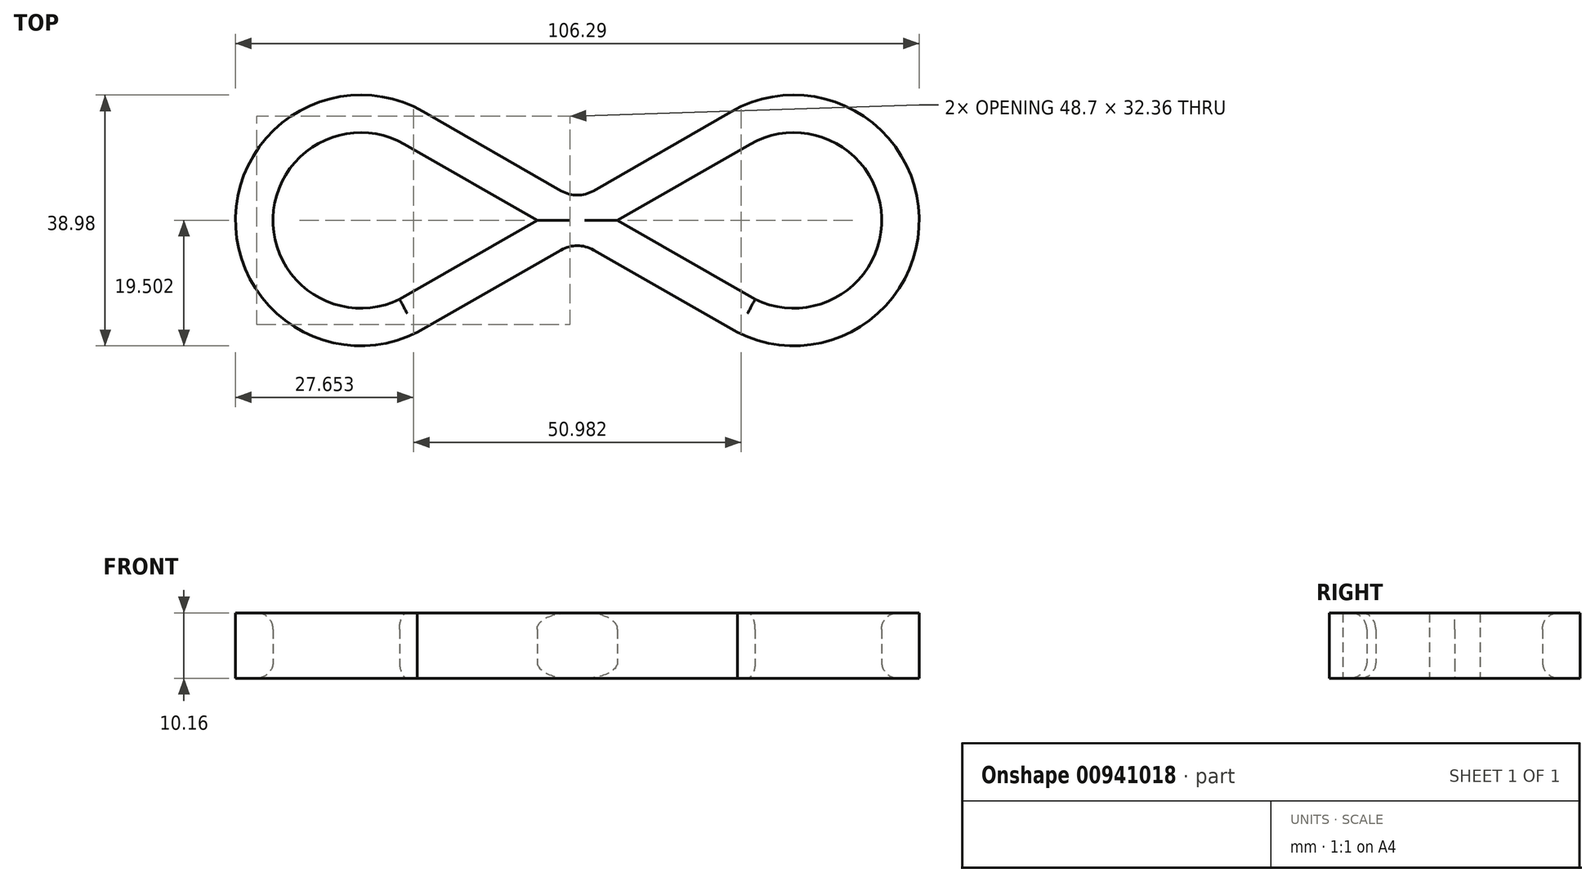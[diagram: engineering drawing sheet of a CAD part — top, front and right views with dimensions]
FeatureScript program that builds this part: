
annotation { "Feature Type Name" : "Feature", "Feature Type Description" : "" }
export const myFeature = defineFeature(function(context is Context, id is Id, definition is map)
    precondition{}
    {
        {
            var Q0;
            Q0=qCreatedBy(makeId("Top.planeOp"),FACE);
            var sketch = newSketch(context, id + "F0", { "sketchPlane" : qUnion([Q0])});
            skArc(sketch, "E0", {"start": v(6.8, 11.84) * mm, "mid": v(-13.64, 0.44) * mm, "end": v(6.02, -12.25) * mm});
            skLineSegment(sketch, "E1", {"start": v(27.4, 0) * mm, "end": v(6.8, 11.84) * mm});
            skLineSegment(sketch, "E2", {"start": v(6.02, -12.25) * mm, "end": v(27.4, 0) * mm});
            skArc(sketch, "E3.0", {"start": v(9.71, 16.9) * mm, "mid": v(-19.49, 0.53) * mm, "end": v(8.77, -17.4) * mm});
            skLineSegment(sketch, "E3.1", {"start": v(33.65, 3.15) * mm, "end": v(9.71, 16.9) * mm});
            skLineSegment(sketch, "E3.2", {"start": v(8.77, -17.4) * mm, "end": v(33.65, -3.15) * mm});
            skLineSegment(sketch, "E4.MirrorCS", {"start": v(33.65, 3.15) * mm, "end": v(57.6, 16.9) * mm});
            skLineSegment(sketch, "E5.MirrorCS", {"start": v(61.3, -12.25) * mm, "end": v(39.9, 0) * mm});
            skLineSegment(sketch, "E6.MirrorCS", {"start": v(58.53, -17.4) * mm, "end": v(33.65, -3.15) * mm});
            skArc(sketch, "E7.MirrorCS", {"start": v(57.6, 16.9) * mm, "mid": v(86.8, 0.53) * mm, "end": v(58.53, -17.4) * mm});
            skArc(sketch, "E8.MirrorCS", {"start": v(60.5, 11.84) * mm, "mid": v(80.95, 0.44) * mm, "end": v(61.3, -12.25) * mm});
            skLineSegment(sketch, "E9.MirrorCS", {"start": v(39.9, 0) * mm, "end": v(60.5, 11.84) * mm});
            skSolve(sketch);
        }
        {
            var Q0;
            Q0 = qSketchRegion(id + "F0", true);
            extrude(context, id + "F1", {"entities" : qUnion([Q0]), "depth" : 10.16 * mm, "offsetDistance" : 25.4 * mm});
        }
        {
            var Q0;
            Q0=makeQuery(id+"F1.opExtrude","CAP_EDGE",EDGE,{"disambiguationData":[OSD([sQuery(id+"F0.wireOp",EDGE,"E8.MirrorCS")])],"isStart":false});
            var Q1;
            Q1=makeQuery(id+"F1.opExtrude","CAP_EDGE",EDGE,{"disambiguationData":[OSD([sQuery(id+"F0.wireOp",EDGE,"E0")])],"isStart":false});
            var Q2;
            Q2=makeQuery(id+"F1.opExtrude","CAP_EDGE",EDGE,{"disambiguationData":[OSD([sQuery(id+"F0.wireOp",EDGE,"E8.MirrorCS")])],"isStart":true});
            var Q3;
            Q3=makeQuery(id+"F1.opExtrude","CAP_EDGE",EDGE,{"disambiguationData":[OSD([sQuery(id+"F0.wireOp",EDGE,"E0")])],"isStart":true});
            fillet(context, id + "F2", {"entities" : qUnion([Q0, Q1, Q2, Q3]), "radius" : 2.54 * mm, "tangentPropagation" : true, "allowEdgeOverflow" : false});
        }
        {
            var Q0;
            Q0=makeQuery(id+"F1.opExtrude","CAP_EDGE",EDGE,{"disambiguationData":[OSD([sQuery(id+"F0.wireOp",EDGE,"E2")])],"isStart":false});
            var Q1;
            Q1=makeQuery(id+"F1.opExtrude","CAP_EDGE",EDGE,{"disambiguationData":[OSD([sQuery(id+"F0.wireOp",EDGE,"E2")])],"isStart":true});
            var Q2;
            Q2=makeQuery(id+"F1.opExtrude","CAP_EDGE",EDGE,{"disambiguationData":[OSD([sQuery(id+"F0.wireOp",EDGE,"E5.MirrorCS")])],"isStart":true});
            var Q3;
            Q3=makeQuery(id+"F1.opExtrude","CAP_EDGE",EDGE,{"disambiguationData":[OSD([sQuery(id+"F0.wireOp",EDGE,"E5.MirrorCS")])],"isStart":false});
            fillet(context, id + "F3", {"entities" : qUnion([Q0, Q1, Q2, Q3]), "radius" : 2.54 * mm, "tangentPropagation" : true, "allowEdgeOverflow" : false});
        }
        {
            var Q0;
            Q0=makeQuery(id+"F1.opExtrude","SWEPT_EDGE",EDGE,{"disambiguationData":[OSD([sQuery(id+"F0.wireOp",EDGE,"E3.2"),sQuery(id+"F0.wireOp",EDGE,"E6.MirrorCS")])]});
            var Q1;
            Q1=makeQuery(id+"F1.opExtrude","SWEPT_EDGE",EDGE,{"disambiguationData":[OSD([sQuery(id+"F0.wireOp",EDGE,"E3.1"),sQuery(id+"F0.wireOp",EDGE,"E4.MirrorCS")])]});
            fillet(context, id + "F4", {"entities" : qUnion([Q0, Q1]), "radius" : 5.08 * mm, "tangentPropagation" : true, "allowEdgeOverflow" : false});
        }
    });
